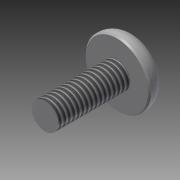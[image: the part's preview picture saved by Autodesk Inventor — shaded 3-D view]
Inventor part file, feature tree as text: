
AUTODESK INVENTOR PART (.ipt)
format: ipt  version: 2013 (Build 170138000, 138)  size: 134,144 bytes
history: native  units: in
note: dims shown in document units (in); Inventor stores cm internally (conversion verified against a paired STEP export)
features: extrude x3, sketch x2, fillet x1, thread x1, chamfer x1
ambient origin geometry x8: Origin, YZ Plane, XZ Plane, XY Plane, X Axis, Y Axis, Z Axis, Center Point
bodies: Solid1 (feature_tree)
feature tree (8):
  sketch  "Sketch1"  dims[d0=0.4538in d2=0.185in]
  extrude  "Extrusion1"  Depth=0.185in
  extrude  "Extrusion2"  Depth=0.1969in
  fillet  "Fillet1"  Radius=0.125in
  extrude  "Extrusion3"  Depth=0.1in
  thread  "Thread1"  [1 undecoded]
  chamfer  "Chamfer1"  Distance=0.075in
  sketch  "Sketch2"  dims[d3=0.5in d4=0.0in d5=0.1969in d6=0.125in d7=0.0in d8=0.1in d9=0.1969in d10=0.075in d11=0.0in d12=1.0in d13=0.0in d14=0.01in d15=0.125in d16=45.0deg]
note: 1 required parameter value undecoded (feature->parameter linkage not recoverable at this tier; creation-order binding heuristic only, values carry confidence <= 0.55)
